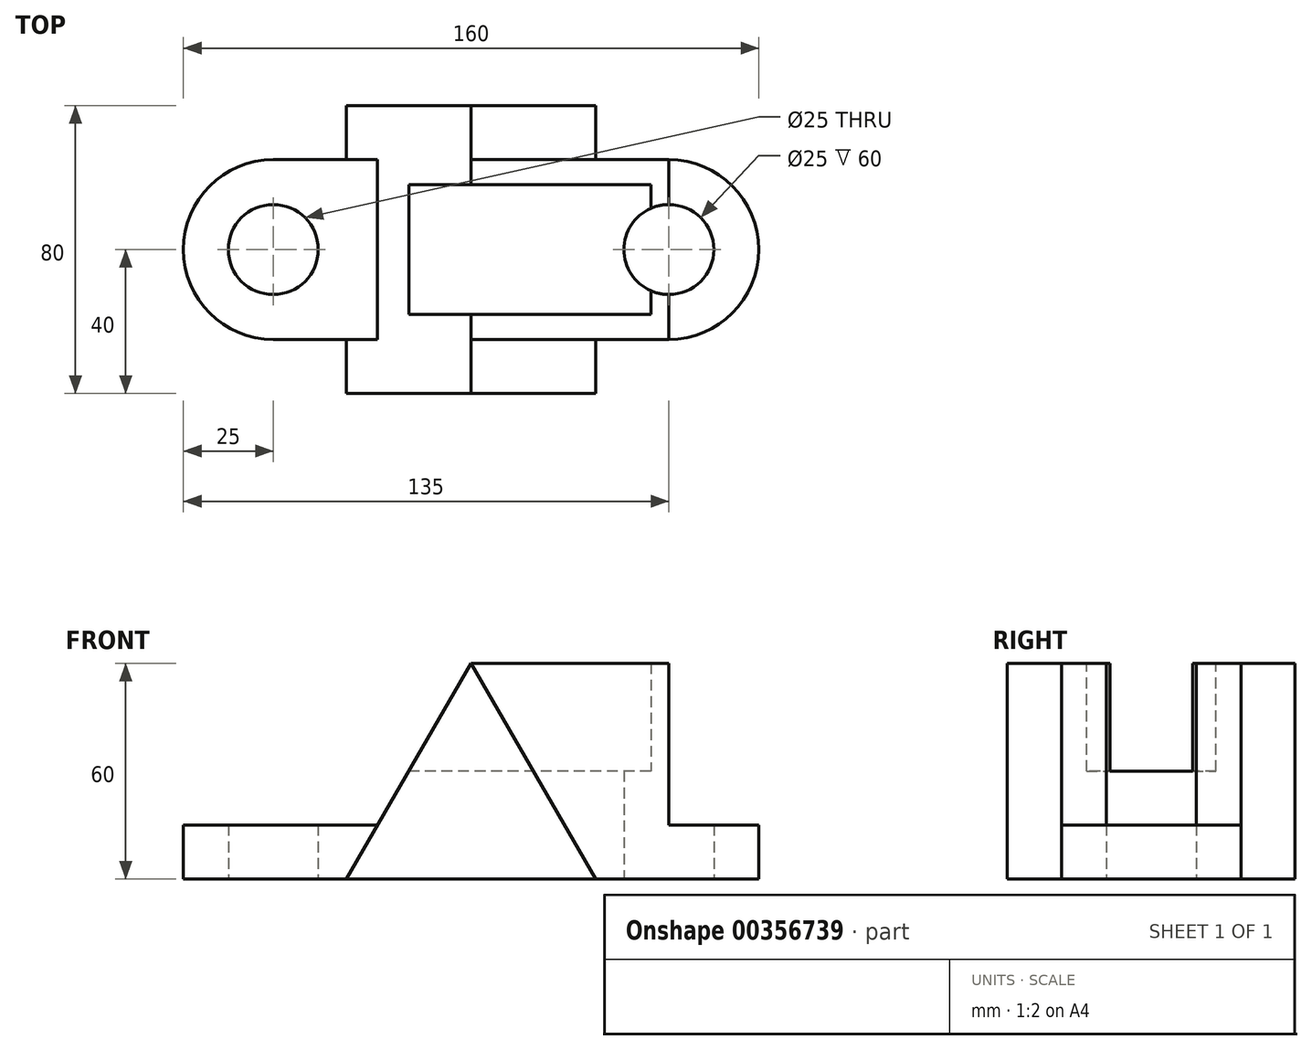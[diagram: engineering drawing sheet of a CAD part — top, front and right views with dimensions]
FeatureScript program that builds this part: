
annotation { "Feature Type Name" : "Feature", "Feature Type Description" : "" }
export const myFeature = defineFeature(function(context is Context, id is Id, definition is map)
    precondition{}
    {
        {
            var Q0;
            Q0=qCreatedBy(makeId("Top.planeOp"),FACE);
            var sketch = newSketch(context, id + "F0", { "sketchPlane" : qUnion([Q0])});
            skLineSegment(sketch, "E0.bottom", {"start": v(55, -25) * mm, "end": v(-55, -25) * mm});
            skLineSegment(sketch, "E0.top", {"start": v(55, 25) * mm, "end": v(-55, 25) * mm});
            skPoint(sketch, "E0.middle", {"position": v(0, 0) * mm});
            skArc(sketch, "E1", {"start": v(55, -25) * mm, "mid": v(80, 0) * mm, "end": v(55, 25) * mm});
            skArc(sketch, "E2", {"start": v(-55, 25) * mm, "mid": v(-80, 0) * mm, "end": v(-55, -25) * mm});
            skCircle(sketch, "E3", {"center": v(-55, 0) * mm, "radius": 12.5 * mm});
            skCircle(sketch, "E4", {"center": v(55, 0) * mm, "radius": 12.5 * mm});
            skSolve(sketch);
        }
        {
            var Q0;
            Q0=makeQuery(id+"F0.imprint","IMPRINT",FACE,{"disambiguationData":[TD([[makeQuery(id+"F0.imprint","IMPRINT",EDGE,{"derivedFrom":sQuery(id+"F0.wireOp",EDGE,"E0.bottom")}),-1.0]])]});
            extrude(context, id + "F1", {"entities" : qUnion([Q0]), "depth" : 60 * mm});
        }
        {
            var Q0;
            Q0=makeQuery(id+"F1.opExtrude","SWEPT_FACE",FACE,{"disambiguationData":[OSD([sQuery(id+"F0.wireOp",EDGE,"E0.bottom")])]});
            var sketch = newSketch(context, id + "F2", { "sketchPlane" : qUnion([Q0])});
            skLineSegment(sketch, "E5", {"start": v(-55, 60) * mm, "end": v(-55, 0) * mm});
            skLineSegment(sketch, "E6", {"start": v(55, 60) * mm, "end": v(55, 0) * mm});
            skLineSegment(sketch, "E7.bottom", {"start": v(-55, 60) * mm, "end": v(-80, 60) * mm});
            skLineSegment(sketch, "E7.top", {"start": v(-55, 0) * mm, "end": v(-80, 0) * mm});
            skLineSegment(sketch, "E7.right", {"start": v(-80, 60) * mm, "end": v(-80, 0) * mm});
            skLineSegment(sketch, "E8.bottom", {"start": v(55, 60) * mm, "end": v(80, 60) * mm});
            skLineSegment(sketch, "E8.top", {"start": v(55, 0) * mm, "end": v(80, 0) * mm});
            skLineSegment(sketch, "E8.right", {"start": v(80, 60) * mm, "end": v(80, 0) * mm});
            skLineSegment(sketch, "E9", {"start": v(0, 60) * mm, "end": v(34.64, 0) * mm});
            skLineSegment(sketch, "E10", {"start": v(34.64, 0) * mm, "end": v(0, 0) * mm});
            skLineSegment(sketch, "E11.MirrorCS", {"start": v(0, 60) * mm, "end": v(-34.64, 0) * mm});
            skLineSegment(sketch, "E12.MirrorCS", {"start": v(-34.64, 0) * mm, "end": v(0, 0) * mm});
            skLineSegment(sketch, "E13", {"start": v(-80, 15) * mm, "end": v(-55, 15) * mm});
            skLineSegment(sketch, "E14", {"start": v(-25.98, 15) * mm, "end": v(-55, 15) * mm});
            skLineSegment(sketch, "E15", {"start": v(55, 15) * mm, "end": v(25.98, 15) * mm});
            skLineSegment(sketch, "E16", {"start": v(25.98, 15) * mm, "end": v(55, 15) * mm});
            skLineSegment(sketch, "E17", {"start": v(80, 15) * mm, "end": v(55, 15) * mm});
            skLineSegment(sketch, "E18", {"start": v(-55, 0) * mm, "end": v(-34.64, 0) * mm});
            skLineSegment(sketch, "E19", {"start": v(34.64, 0) * mm, "end": v(55, 0) * mm});
            skSolve(sketch);
        }
        {
            var Q0;
            {var subQ0=sQuery(id+"F2.wireOp",EDGE,"E7.bottom");Q0=makeQuery(id+"F2.imprint","IMPRINT",FACE,{"disambiguationData":[TD([[makeQuery(id+"F2.imprint","IMPRINT",EDGE,{"derivedFrom":subQ0}),1.0]])]});}
            var Q1;
            {var subQ3=sQuery(id+"F2.wireOp",EDGE,"E14");Q1=makeQuery(id+"F2.imprint","IMPRINT",FACE,{"disambiguationData":[TD([[makeQuery(id+"F2.imprint","IMPRINT",EDGE,{"derivedFrom":subQ3}),-1.0]])]});}
            var Q2;
            {var subQ3=sQuery(id+"F2.wireOp",EDGE,"E16");Q2=makeQuery(id+"F2.imprint","IMPRINT",FACE,{"disambiguationData":[TD([[makeQuery(id+"F2.imprint","IMPRINT",EDGE,{"derivedFrom":subQ3}),1.0]])]});}
            var Q3;
            {var subQ0=sQuery(id+"F2.wireOp",EDGE,"E8.bottom");Q3=makeQuery(id+"F2.imprint","IMPRINT",FACE,{"disambiguationData":[TD([[makeQuery(id+"F2.imprint","IMPRINT",EDGE,{"derivedFrom":subQ0}),-1.0]])]});}
            extrude(context, id + "F3", {"entities" : qUnion([Q0, Q1, Q2, Q3]), "operationType" : NewBodyOperationType.REMOVE, "oppositeDirection" : true, "depth" : 80 * mm});
        }
        {
            var Q0;
            {var subQ4=sQuery(id+"F2.wireOp",EDGE,"E10");Q0=makeQuery(id+"F2.imprint","IMPRINT",FACE,{"disambiguationData":[TD([[makeQuery(id+"F2.imprint","IMPRINT",EDGE,{"derivedFrom":subQ4}),-1.0]])]});}
            extrude(context, id + "F4", {"entities" : qUnion([Q0]), "operationType" : NewBodyOperationType.ADD, "depth" : 15 * mm});
        }
        {
            var Q0;
            Q0=makeQuery(id+"F1.opExtrude","SWEPT_FACE",FACE,{"disambiguationData":[OSD([sQuery(id+"F0.wireOp",EDGE,"E0.top")])]});
            var sketch = newSketch(context, id + "F5", { "sketchPlane" : qUnion([Q0])});
            skLineSegment(sketch, "E20", {"start": v(0, 60) * mm, "end": v(34.64, 0) * mm});
            skLineSegment(sketch, "E21", {"start": v(0, 60) * mm, "end": v(-34.64, 0) * mm});
            skLineSegment(sketch, "E22", {"start": v(34.64, 0) * mm, "end": v(-34.64, 0) * mm});
            skSolve(sketch);
        }
        {
            var Q0;
            {var subQ4=sQuery(id+"F5.wireOp",EDGE,"E22");Q0=makeQuery(id+"F5.imprint","IMPRINT",FACE,{"disambiguationData":[TD([[makeQuery(id+"F5.imprint","IMPRINT",EDGE,{"derivedFrom":subQ4}),1.0]])]});}
            extrude(context, id + "F6", {"entities" : qUnion([Q0]), "operationType" : NewBodyOperationType.ADD, "depth" : 15 * mm});
        }
        {
            var Q0;
            Q0=qCreatedBy(makeId("Right.planeOp"),FACE);
            var sketch = newSketch(context, id + "F7", { "sketchPlane" : qUnion([Q0])});
            skLineSegment(sketch, "E23.bottom", {"start": v(-18, 60) * mm, "end": v(18, 60) * mm});
            skLineSegment(sketch, "E23.top", {"start": v(-18, 30) * mm, "end": v(18, 30) * mm});
            skLineSegment(sketch, "E23.left", {"start": v(-18, 60) * mm, "end": v(-18, 30) * mm});
            skLineSegment(sketch, "E23.right", {"start": v(18, 60) * mm, "end": v(18, 30) * mm});
            skSolve(sketch);
        }
        {
            var Q0;
            Q0 = qSketchRegion(id + "F7", true);
            var Q1;
            Q1=sQuery(id+"F7.wireOp",EDGE,"E23.top");
            var Q2;
            Q2=sQuery(id+"F7.wireOp",EDGE,"E23.right");
            var Q3;
            Q3=sQuery(id+"F7.wireOp",EDGE,"E23.bottom");
            var Q4;
            Q4=sQuery(id+"F7.wireOp",EDGE,"E23.left");
            extrude(context, id + "F8", {"entities" : qUnion([Q0]), "operationType" : NewBodyOperationType.REMOVE, "surfaceEntities" : qUnion([Q1, Q2, Q3, Q4]), "depth" : 50 * mm});
        }
        {
            var Q0;
            Q0=makeQuery(id+"F8.boolean.opBoolean","COPY",FACE,{"derivedFrom":makeQuery(id+"F8.opExtrude","CAP_FACE",FACE,{"disambiguationData":[OSD([sQuery(id+"F7.wireOp",EDGE,"E23.bottom"),sQuery(id+"F7.wireOp",EDGE,"E23.top"),sQuery(id+"F7.wireOp",EDGE,"E23.left"),sQuery(id+"F7.wireOp",EDGE,"E23.right")])],"isStart":true})});
            extrude(context, id + "F9", {"entities" : qUnion([Q0]), "operationType" : NewBodyOperationType.REMOVE, "oppositeDirection" : true, "depth" : 25 * mm});
        }
    });
